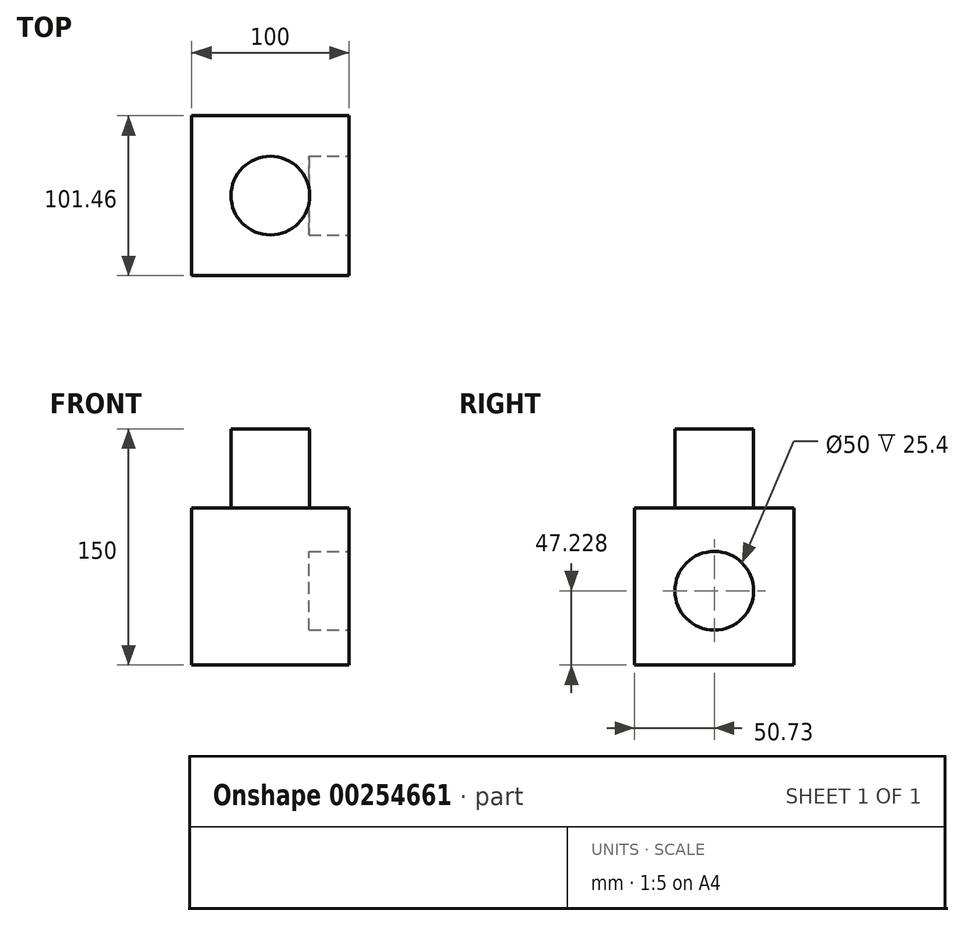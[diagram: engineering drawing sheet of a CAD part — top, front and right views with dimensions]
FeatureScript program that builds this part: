
annotation { "Feature Type Name" : "Feature", "Feature Type Description" : "" }
export const myFeature = defineFeature(function(context is Context, id is Id, definition is map)
    precondition{}
    {
        {
            var Q0;
            Q0=qCreatedBy(makeId("Top.planeOp"),FACE);
            var sketch = newSketch(context, id + "F0", { "sketchPlane" : qUnion([Q0])});
            skLineSegment(sketch, "E0.bottom", {"start": v(50, 50.73) * mm, "end": v(-50, 50.73) * mm});
            skLineSegment(sketch, "E0.top", {"start": v(50, -50.73) * mm, "end": v(-50, -50.73) * mm});
            skLineSegment(sketch, "E0.left", {"start": v(50, 50.73) * mm, "end": v(50, -50.73) * mm});
            skLineSegment(sketch, "E0.right", {"start": v(-50, 50.73) * mm, "end": v(-50, -50.73) * mm});
            skPoint(sketch, "E0.middle", {"position": v(0, 0) * mm});
            skSolve(sketch);
        }
        {
            var Q0;
            Q0 = qSketchRegion(id + "F0", true);
            extrude(context, id + "F1", {"entities" : qUnion([Q0]), "depth" : 100 * mm});
        }
        {
            var Q0;
            Q0=makeQuery(id+"F1.opExtrude","CAP_FACE",FACE,{"disambiguationData":[OSD([sQuery(id+"F0.wireOp",EDGE,"E0.bottom"),sQuery(id+"F0.wireOp",EDGE,"E0.top"),sQuery(id+"F0.wireOp",EDGE,"E0.left"),sQuery(id+"F0.wireOp",EDGE,"E0.right")])],"isStart":false});
            var sketch = newSketch(context, id + "F2", { "sketchPlane" : qUnion([Q0])});
            skCircle(sketch, "E1", {"center": v(0, 0) * mm, "radius": 25 * mm});
            skSolve(sketch);
        }
        {
            var Q0;
            Q0 = qSketchRegion(id + "F2", true);
            extrude(context, id + "F3", {"entities" : qUnion([Q0]), "operationType" : NewBodyOperationType.ADD, "depth" : 50 * mm});
        }
        {
            var Q0;
            Q0=qCreatedBy(makeId("Top.planeOp"),FACE);
            var sketch = newSketch(context, id + "F4", { "sketchPlane" : qUnion([Q0])});
            skCircle(sketch, "E2", {"center": v(0, 0) * mm, "radius": 25 * mm});
            skSolve(sketch);
        }
        {
            var Q0;
            Q0 = qSketchRegion(id + "F4", true);
            extrude(context, id + "F5", {"entities" : qUnion([Q0]), "operationType" : NewBodyOperationType.ADD, "depth" : 50 * mm});
        }
        {
            var Q0;
            Q0=sQuery(id+"F4.wireOp",EDGE,"E2");
            extrude(context, id + "F6", {"bodyType" : ToolBodyType.SURFACE, "surfaceEntities" : qUnion([Q0]), "depth" : 25.4 * mm});
        }
        {
            var Q0;
            Q0=makeQuery(id+"F4.imprint","IMPRINT",FACE,{"disambiguationData":[TD([[makeQuery(id+"F4.imprint","IMPRINT",EDGE,{"derivedFrom":sQuery(id+"F4.wireOp",EDGE,"E2")}),1.0]])]});
            extrude(context, id + "F7", {"entities" : qUnion([Q0]), "operationType" : NewBodyOperationType.ADD, "depth" : 25.4 * mm});
        }
        {
            var Q0;
            Q0=makeQuery(id+"F1.opExtrude","SWEPT_FACE",FACE,{"disambiguationData":[OSD([sQuery(id+"F0.wireOp",EDGE,"E0.left")])]});
            var sketch = newSketch(context, id + "F8", { "sketchPlane" : qUnion([Q0])});
            skCircle(sketch, "E3", {"center": v(0, 47.23) * mm, "radius": 25 * mm});
            skSolve(sketch);
        }
        {
            var Q0;
            Q0 = qSketchRegion(id + "F8", true);
            extrude(context, id + "F9", {"entities" : qUnion([Q0]), "operationType" : NewBodyOperationType.REMOVE, "oppositeDirection" : true, "depth" : 25.4 * mm});
        }
    });
